# Revit family: 27470-presto
name_source: partatom
category: Plumbing Fixtures
units: mm (PartAtom-declared; Revit-internal decimal feet)

## family parameters
Always vertical = Yes
Cut with Voids When Loaded = No
Maintain Annotation Orientation = No
Part Type = Normal
Room Calculation Point = No
Round Connector Dimension = Use Diameter
Shared = No
Work Plane-Based = Yes

## types (1)
- 27470-presto
    - Hydraulic supply = 12.50 mm
    Default Elevation = 1219 mm
    Description = Single electronic / sensor shower tap with battery without stop valve
    Manufacturer = presto
    Model = 27470
    RANGE = Shower - DL 400 E SENSOR
    Recommended pressure = 3.0 bar
    URL = https://www.prestodatashare.com
    brand = LES ROBINETS PRESTO
    flow = 6.0 L/min
    flow time = 20.0 s
    min flow = 4.0 L/min
    min pressure = 1.0 bar
    pressure = 5.0 bar
    ref = 27470 - Single electronic / sensor shower tap with battery without stop valve

## geometry (parser evidence)
native form markers: Sweep x2
no freeform markers — native parametric forms only
